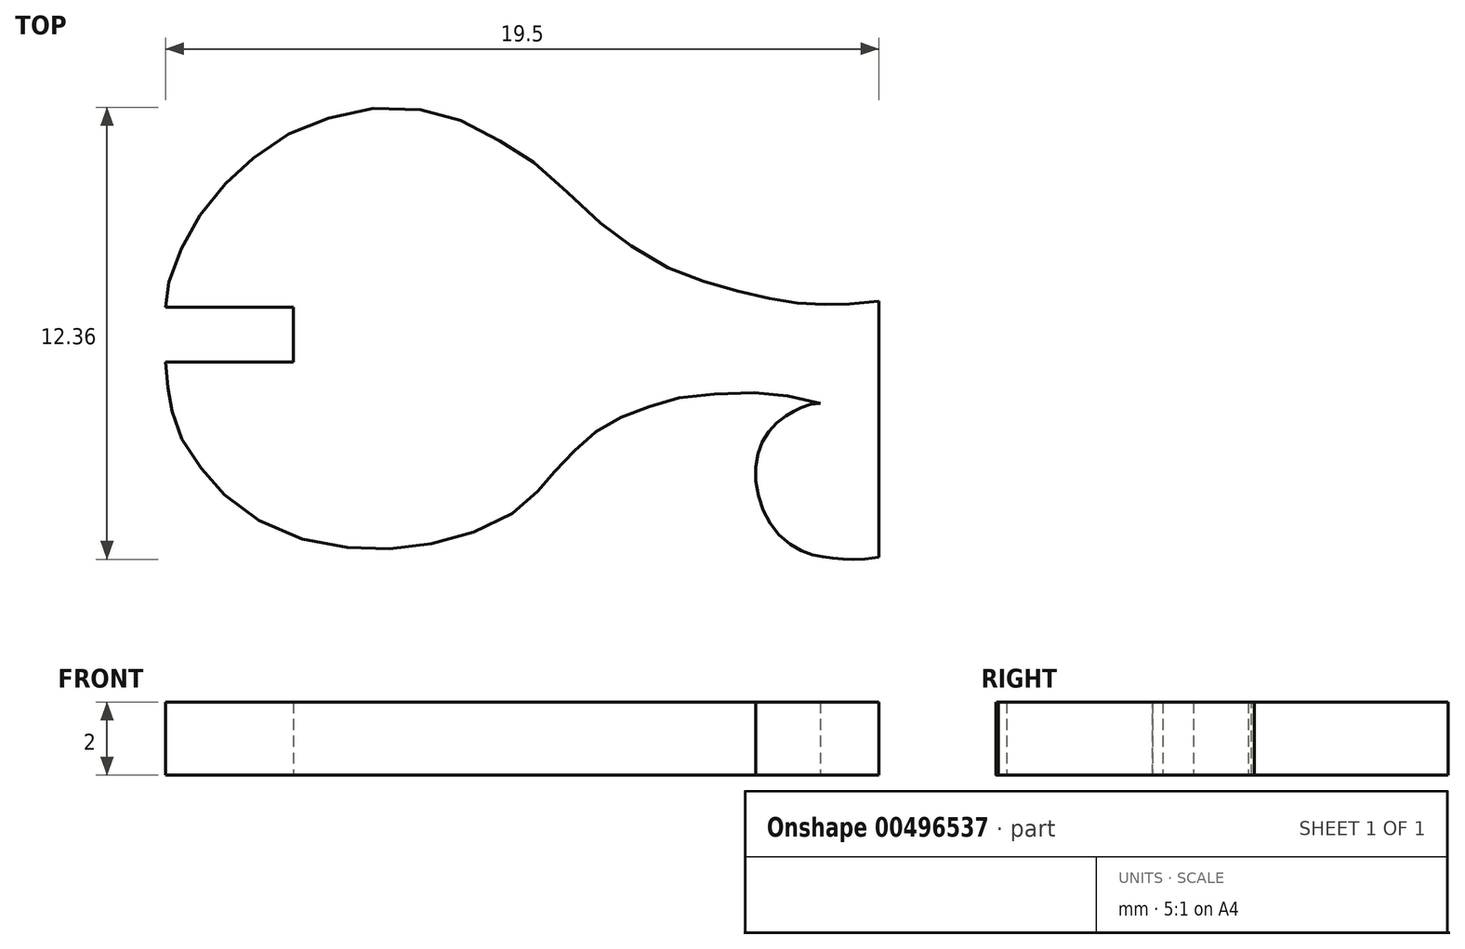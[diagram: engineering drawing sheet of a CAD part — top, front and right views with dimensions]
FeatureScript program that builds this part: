
annotation { "Feature Type Name" : "Feature", "Feature Type Description" : "" }
export const myFeature = defineFeature(function(context is Context, id is Id, definition is map)
    precondition{}
    {
        {
            var Q0;
            Q0=qCreatedBy(makeId("Top.planeOp"),FACE);
            var sketch = newSketch(context, id + "F0", { "sketchPlane" : qUnion([Q0])});
            skLineSegment(sketch, "E0", {"start": v(25.5, 37.3) * mm, "end": v(29, 37.3) * mm});
            skLineSegment(sketch, "E1", {"start": v(29, 37.3) * mm, "end": v(29, 38.8) * mm});
            skLineSegment(sketch, "E2", {"start": v(29, 38.8) * mm, "end": v(25.5, 38.8) * mm});
            skFitSpline(sketch, "E3", {"points": [v(25.5, 38.8) * mm, v(25.55, 39.17) * mm, v(25.67, 39.71) * mm, v(26.03, 40.59) * mm, v(26.53, 41.42) * mm, v(27.25, 42.28) * mm, v(27.94, 42.89) * mm, v(28.96, 43.58) * mm, v(30.12, 44) * mm, v(31.52, 44.25) * mm, v(32.93, 44.11) * mm, v(33.94, 43.73) * mm, v(35.1, 43.06) * mm, v(35.89, 42.5) * mm, v(37.05, 41.4) * mm, v(37.79, 40.8) * mm, v(38.7, 40.17) * mm, v(39.75, 39.65) * mm, v(40.51, 39.43) * mm, v(41.33, 39.18) * mm, v(42, 39.03) * mm, v(42.54, 38.94) * mm, v(43.06, 38.88) * mm, v(43.55, 38.87) * mm, v(43.95, 38.88) * mm, v(44.38, 38.89) * mm, v(45, 38.96) * mm], "startDerivative": vector(3.07, 13.12) * mm, "endDerivative": vector(35, 2.69) * mm});
            skLineSegment(sketch, "E4", {"start": v(45, 38.96) * mm, "end": v(45, 31.96) * mm});
            skFitSpline(sketch, "E5", {"points": [v(45, 31.96) * mm, v(44.18, 31.9) * mm, v(43.63, 31.95) * mm, v(43.04, 32.08) * mm, v(42.25, 32.6) * mm, v(41.7, 33.64) * mm, v(41.68, 34.7) * mm, v(42.03, 35.44) * mm, v(42.54, 35.87) * mm, v(42.9, 36.06) * mm, v(43.4, 36.17) * mm], "startDerivative": vector(-10.12, -1.63) * mm, "endDerivative": vector(5.63, -0.2) * mm});
            skFitSpline(sketch, "E6", {"points": [v(25.5, 37.3) * mm, v(25.54, 36.82) * mm, v(25.64, 36.18) * mm, v(25.7, 35.87) * mm, v(25.99, 35.13) * mm, v(26.56, 34.3) * mm, v(27.28, 33.53) * mm, v(28.67, 32.65) * mm, v(30.38, 32.24) * mm, v(31.83, 32.2) * mm, v(33.27, 32.45) * mm, v(34.74, 33) * mm, v(35.58, 33.66) * mm, v(35.94, 34.08) * mm, v(36.36, 34.54) * mm, v(36.86, 35.04) * mm, v(37.36, 35.45) * mm, v(37.95, 35.77) * mm, v(38.65, 36.04) * mm, v(39.39, 36.28) * mm, v(40.31, 36.4) * mm, v(41.62, 36.46) * mm, v(42.52, 36.36) * mm, v(43.4, 36.17) * mm], "startDerivative": vector(0.64, -16.17) * mm, "endDerivative": vector(22.25, -5.13) * mm});
            skSolve(sketch);
        }
        {
            var Q0;
            Q0=qSketchRegion(id+"F0",true);
            extrude(context, id + "F1", {"entities" : qUnion([Q0]), "depth" : 2 * mm, "offsetDistance" : 25 * mm});
        }
    });
